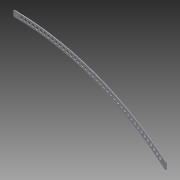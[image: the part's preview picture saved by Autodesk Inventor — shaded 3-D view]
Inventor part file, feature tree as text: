
AUTODESK INVENTOR PART (.ipt)
format: ipt  version: 2014 (Build 180170000, 170)  size: 183,808 bytes
history: native  units: in
note: dims shown in document units (in); Inventor stores cm internally (conversion verified against a paired STEP export)
features: extrude x3, sketch x3
ambient origin geometry x8: Origin, YZ Plane, XZ Plane, XY Plane, X Axis, Y Axis, Z Axis, Center Point
bodies: Solid1 (feature_tree)
feature tree (6):
  extrude  "Extrusion1"  Depth=4.0in
  extrude  "Extrusion2"  Depth=5.0in
  extrude  "Extrusion3"  Depth=0.125in
  sketch  "Sketch1"  dims[d2=13.5in d3=4.0in]
  sketch  "Sketch2"  dims[d4=1.75in d6=5.0in]
  sketch  "Sketch3"  dims[d7=1.0in d9=0.125in d10=0.125in d11=0.0in d12=0.163in d13=0.5in d14=3.5in d15=0.163in d17=6.5in d18=1.0in d19=0.0in d20=27.0in d21=25.875in d22=0.125in d23=26.5in d24=0.5in d25=41.26in d26=0.0137in d27=0.2762in d28=15.748in d30=0.2542in d32=1.0in d33=0.0in]
